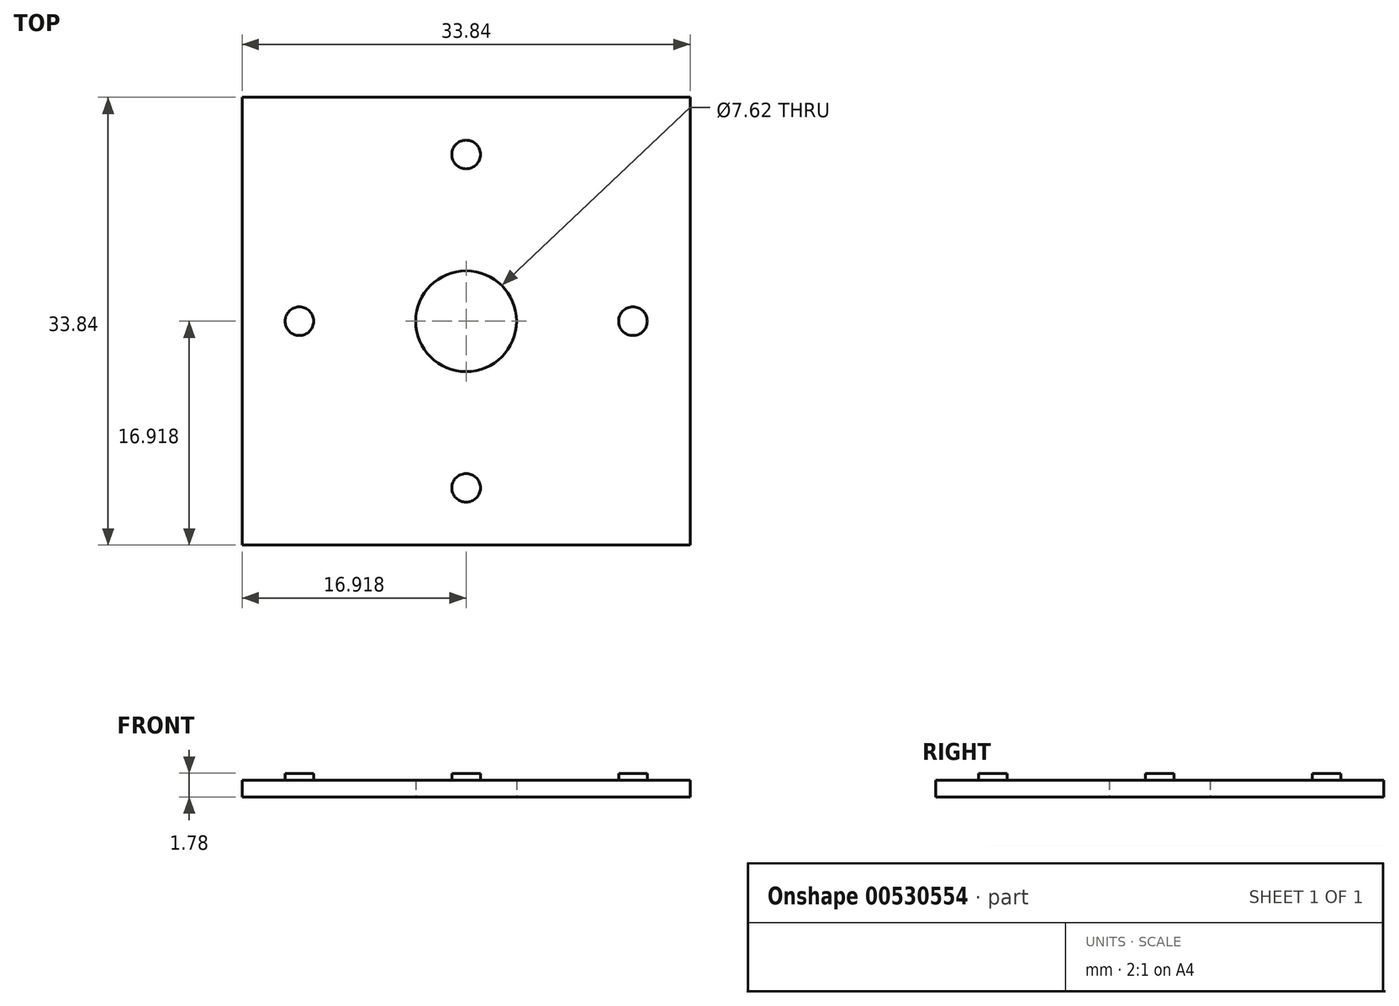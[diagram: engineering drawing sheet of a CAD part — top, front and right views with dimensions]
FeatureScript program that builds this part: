
annotation { "Feature Type Name" : "Feature", "Feature Type Description" : "" }
export const myFeature = defineFeature(function(context is Context, id is Id, definition is map)
    precondition{}
    {
        {
            var Q0;
            Q0=qCreatedBy(makeId("Top.planeOp"),FACE);
            var sketch = newSketch(context, id + "F0", { "sketchPlane" : qUnion([Q0])});
            skLineSegment(sketch, "E0.bottom", {"start": v(0, 0) * mm, "end": v(33.84, 0) * mm});
            skLineSegment(sketch, "E0.top", {"start": v(0, 33.84) * mm, "end": v(33.84, 33.84) * mm});
            skLineSegment(sketch, "E0.left", {"start": v(0, 0) * mm, "end": v(0, 33.84) * mm});
            skLineSegment(sketch, "E0.right", {"start": v(33.84, 0) * mm, "end": v(33.84, 33.84) * mm});
            skCircle(sketch, "E1", {"center": v(16.92, 16.92) * mm, "radius": 3.81 * mm});
            skPoint(sketch, "E2", {"position": v(16.92, 28.58) * mm});
            skPoint(sketch, "E3", {"position": v(5.26, 16.92) * mm});
            skPoint(sketch, "E4", {"position": v(28.58, 16.92) * mm});
            skPoint(sketch, "E5", {"position": v(16.92, 5.26) * mm});
            skSolve(sketch);
        }
        {
            var Q0;
            Q0 = qSketchRegion(id + "F0", true);
            extrude(context, id + "F1", {"entities" : qUnion([Q0]), "depth" : 1.27 * mm, "offsetDistance" : 25.4 * mm});
        }
        {
            var Q0;
            Q0=makeQuery(id+"F1.opExtrude","CAP_FACE",FACE,{"disambiguationData":[OSD([sQuery(id+"F0.wireOp",EDGE,"E0.bottom"),sQuery(id+"F0.wireOp",EDGE,"E0.top"),sQuery(id+"F0.wireOp",EDGE,"E0.left"),sQuery(id+"F0.wireOp",EDGE,"E0.right"),sQuery(id+"F0.wireOp",EDGE,"E1")])],"isStart":false});
            var sketch = newSketch(context, id + "F2", { "sketchPlane" : qUnion([Q0])});
            skCircle(sketch, "E6", {"center": v(29.52, 16.92) * mm, "radius": 1.08 * mm});
            skCircle(sketch, "E7.MirrorC", {"center": v(4.32, 16.92) * mm, "radius": 1.08 * mm});
            skCircle(sketch, "E8", {"center": v(16.92, 29.52) * mm, "radius": 1.08 * mm});
            skCircle(sketch, "E9.MirrorC", {"center": v(16.92, 4.32) * mm, "radius": 1.08 * mm});
            skSolve(sketch);
        }
        {
            var Q0;
            Q0 = qSketchRegion(id + "F2", true);
            extrude(context, id + "F3", {"entities" : qUnion([Q0]), "operationType" : NewBodyOperationType.ADD, "depth" : 0.5 * mm, "offsetDistance" : 25.4 * mm});
        }
    });
